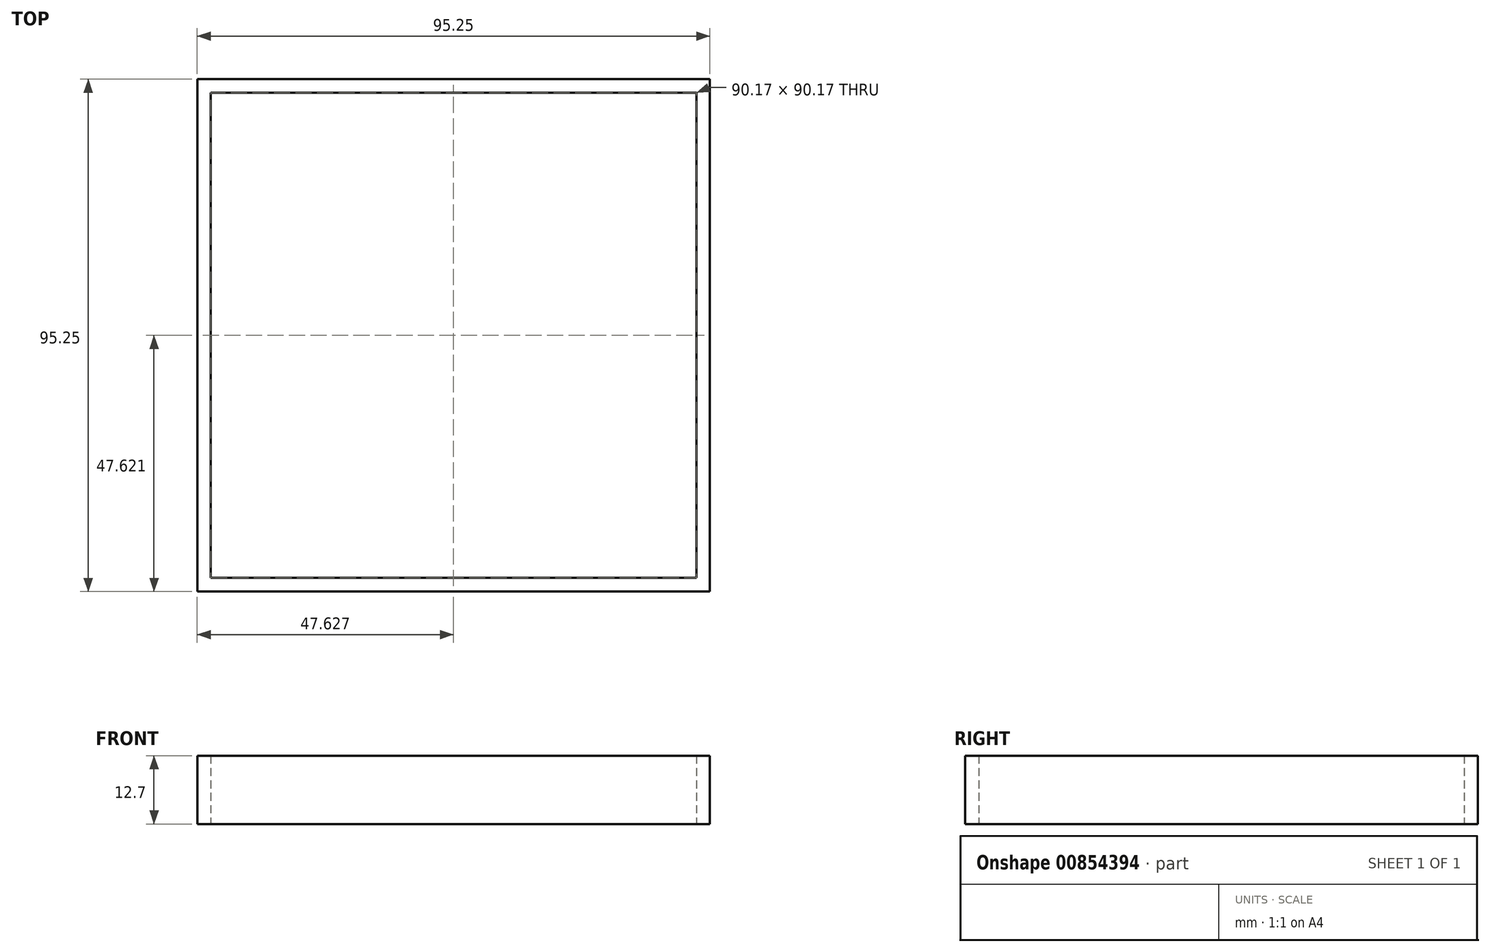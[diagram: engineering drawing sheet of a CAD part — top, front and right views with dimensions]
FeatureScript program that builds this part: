
annotation { "Feature Type Name" : "Feature", "Feature Type Description" : "" }
export const myFeature = defineFeature(function(context is Context, id is Id, definition is map)
    precondition{}
    {
        {
            var Q0;
            Q0=qCreatedBy(makeId("Top.planeOp"),FACE);
            var sketch = newSketch(context, id + "F0", { "sketchPlane" : qUnion([Q0])});
            skLineSegment(sketch, "E0.bottom", {"start": v(-47.8, 59.6) * mm, "end": v(47.45, 59.6) * mm});
            skLineSegment(sketch, "E0.top", {"start": v(-47.8, -35.64) * mm, "end": v(47.45, -35.64) * mm});
            skLineSegment(sketch, "E0.left", {"start": v(-47.8, 59.6) * mm, "end": v(-47.8, -35.64) * mm});
            skLineSegment(sketch, "E0.right", {"start": v(47.45, 59.6) * mm, "end": v(47.45, -35.64) * mm});
            skLineSegment(sketch, "E1.0", {"start": v(-45.26, 57.07) * mm, "end": v(44.91, 57.07) * mm});
            skLineSegment(sketch, "E1.1", {"start": v(-45.26, 57.07) * mm, "end": v(-45.26, -33.1) * mm});
            skLineSegment(sketch, "E1.2", {"start": v(-45.26, -33.1) * mm, "end": v(44.91, -33.1) * mm});
            skLineSegment(sketch, "E1.3", {"start": v(44.91, 57.07) * mm, "end": v(44.91, -33.1) * mm});
            skSolve(sketch);
        }
        {
            var Q0;
            Q0=makeQuery(id+"F0.imprint","IMPRINT",FACE,{"disambiguationData":[TD([[makeQuery(id+"F0.imprint","IMPRINT",EDGE,{"derivedFrom":sQuery(id+"F0.wireOp",EDGE,"E0.bottom")}),-1.0]])]});
            extrude(context, id + "F1", {"entities" : qUnion([Q0]), "depth" : 12.7 * mm, "offsetDistance" : 25.4 * mm});
        }
    });
